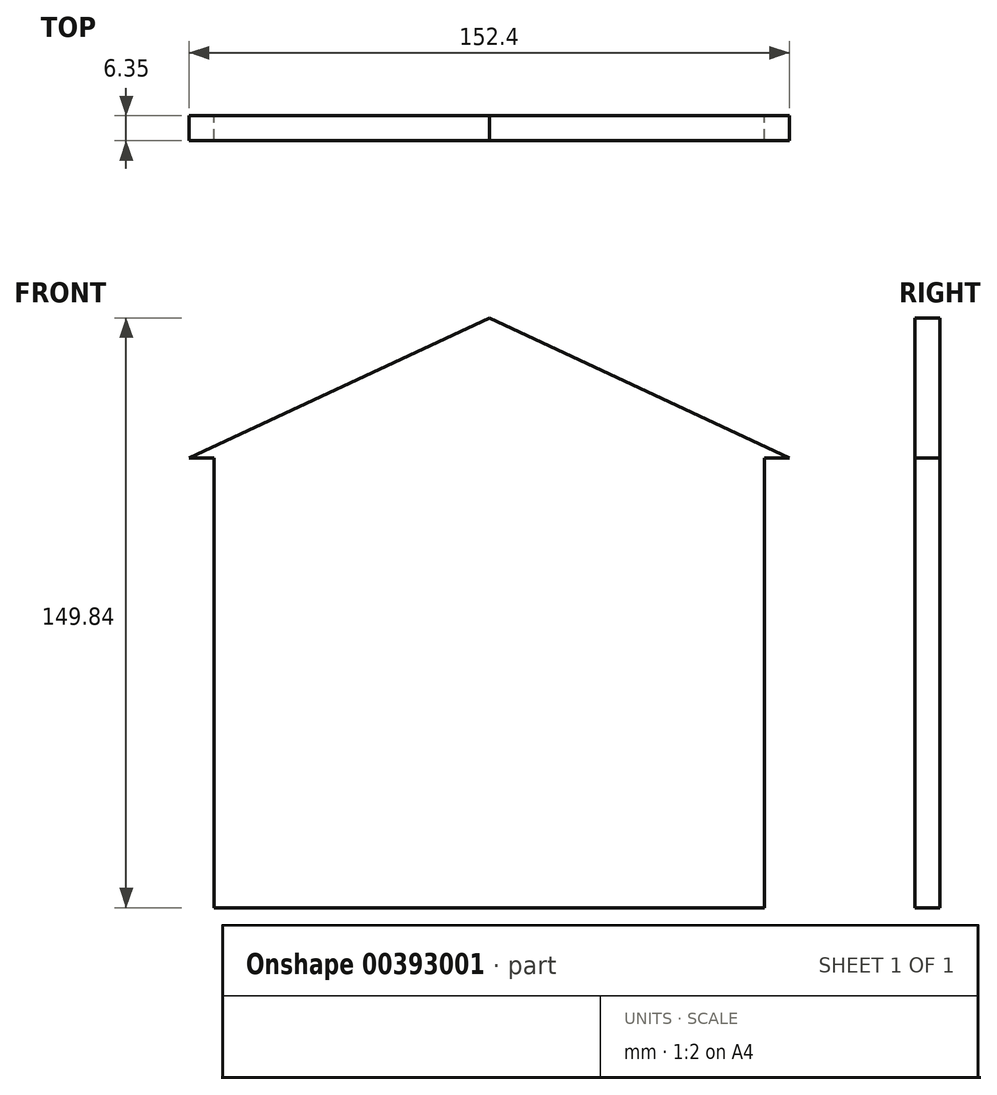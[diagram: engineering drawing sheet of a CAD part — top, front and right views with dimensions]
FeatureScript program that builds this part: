
annotation { "Feature Type Name" : "Feature", "Feature Type Description" : "" }
export const myFeature = defineFeature(function(context is Context, id is Id, definition is map)
    precondition{}
    {
        {
            var Q0;
            Q0=qCreatedBy(makeId("Front.planeOp"),FACE);
            var sketch = newSketch(context, id + "F0", { "sketchPlane" : qUnion([Q0])});
            skLineSegment(sketch, "E0.top", {"start": v(-77.13, -62.46) * mm, "end": v(62.57, -62.46) * mm});
            skLineSegment(sketch, "E0.left", {"start": v(-77.13, 51.84) * mm, "end": v(-77.13, -62.46) * mm});
            skLineSegment(sketch, "E0.right", {"start": v(62.57, 51.84) * mm, "end": v(62.57, -62.46) * mm});
            skLineSegment(sketch, "E1", {"start": v(-77.13, 51.84) * mm, "end": v(-83.48, 51.84) * mm});
            skLineSegment(sketch, "E2", {"start": v(62.57, 51.84) * mm, "end": v(68.92, 51.84) * mm});
            skLineSegment(sketch, "E3", {"start": v(-7.28, -62.46) * mm, "end": v(-7.28, 87.38) * mm, "construction": true});
            skLineSegment(sketch, "E4", {"start": v(-83.48, 51.84) * mm, "end": v(-7.28, 87.38) * mm});
            skLineSegment(sketch, "E5", {"start": v(-7.28, 87.38) * mm, "end": v(68.92, 51.84) * mm});
            skSolve(sketch);
        }
        {
            var Q0;
            Q0=makeQuery(id+"F0.imprint","IMPRINT",FACE,{"disambiguationData":[TD([[makeQuery(id+"F0.imprint","IMPRINT",EDGE,{"derivedFrom":sQuery(id+"F0.wireOp",EDGE,"E0.top")}),1.0]])]});
            extrude(context, id + "F1", {"entities" : qUnion([Q0]), "depth" : 6.35 * mm});
        }
    });
